# Revit family: Haworth_Zody_Counter_Stool_Task_EU_PRELIMINARY
name_source: partatom
category: Furniture
revit_build: Autodesk Revit 2018 (Build: 20170223_1515(x64)
units: mm (PartAtom-declared; Revit-internal decimal feet)

## family parameters
Always vertical = Yes
Cut with Voids When Loaded = No
OmniClass Number = 23.40.70.14.64.11
OmniClass Title = Office Furniture
Room Calculation Point = No
Shared = No
Work Plane-Based = No

## types (3) — shared parameters
Assembly Code = E2020200
Caster Finish = Haworth _ Polymer _ Black
Depth = 74 cm
Description = Haworth - Zody - Counter - Stool - Task
Footring Finish = Haworth _ Metal _ Brushed Aluminum
Hardware Finish = Haworth _ Paint _ Black
Lumbar Finish = Haworth _ Polymer _ Slate
Manufacturer = Haworth
Model = 8969
Revision Number = 1
Size = Verify Final Dim w/Haworth
Support Finish = Haworth _ Metal _ Stainless Steel
Sustainability Info = https://www.haworth.com
URL = https://www.haworth.com
URL - Product = https://www.haworth.com
Warranty = http://www.haworth.com
Width = 74 cm

## per-type parameters (varying)
| type | 4D Arms | Arms |
| Height Adjustable Arms | No | Yes |
| Without Arms | No | No |
| 4D Arms | Yes | Yes |

type visibility flags (boolean, named after types; folded from table):
- Height Adjustable Arms: Yes: Height Adjustable Arms
- Without Arms: Yes: Without Arms
- 4D Arms: Yes: (none)

## geometry (parser evidence)
native form markers: Blend x9, Sweep x13
no freeform markers — native parametric forms only
